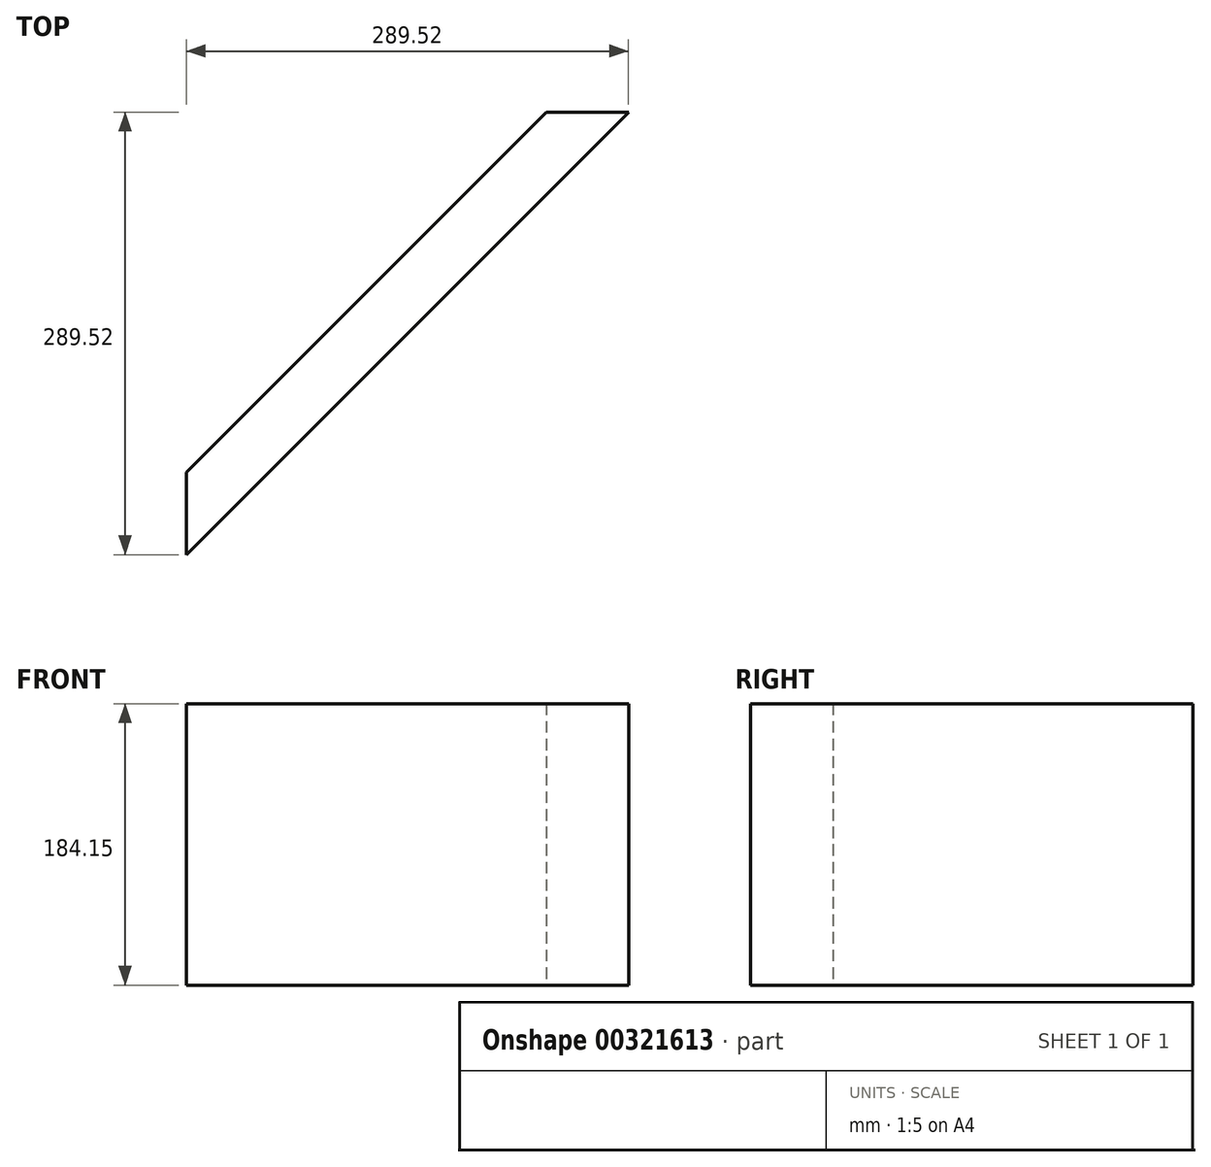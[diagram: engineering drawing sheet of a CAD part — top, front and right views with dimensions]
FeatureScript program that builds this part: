
annotation { "Feature Type Name" : "Feature", "Feature Type Description" : "" }
export const myFeature = defineFeature(function(context is Context, id is Id, definition is map)
    precondition{}
    {
        {
            var Q0;
            Q0=qCreatedBy(makeId("Top.planeOp"),FACE);
            var sketch = newSketch(context, id + "F0", { "sketchPlane" : qUnion([Q0])});
            skLineSegment(sketch, "E0", {"start": v(-54.15, -49.37) * mm, "end": v(-54.15, -103.25) * mm});
            skLineSegment(sketch, "E1", {"start": v(-54.15, -103.25) * mm, "end": v(235.37, 186.27) * mm});
            skLineSegment(sketch, "E2", {"start": v(235.37, 186.27) * mm, "end": v(181.5, 186.27) * mm});
            skLineSegment(sketch, "E3", {"start": v(181.5, 186.27) * mm, "end": v(-54.15, -49.37) * mm});
            skSolve(sketch);
        }
        {
            var Q0;
            Q0=makeQuery(id+"F0.imprint","IMPRINT",FACE,{"disambiguationData":[TD([[makeQuery(id+"F0.imprint","IMPRINT",EDGE,{"derivedFrom":sQuery(id+"F0.wireOp",EDGE,"E0")}),1.0]])]});
            extrude(context, id + "F1", {"entities" : qUnion([Q0]), "depth" : 184.15 * mm});
        }
    });
